# Revit family: Pump_Commercial-Effluent-Zoeller-6150_Seroes
name_source: partatom
category: Mechanical Equipment
revit_build: Autodesk Revit 2018 (Build: 20170223_1515(x64)
units: mm (PartAtom-declared; Revit-internal decimal feet)

## family parameters
Always vertical = No
Classification = None
Cut with Voids When Loaded = No
OmniClass Number = 23.60.30.21
OmniClass Title = Pumps
Part Type = Normal
Room Calculation Point = No
Round Connector Dimension = Use Radius
Shared = Yes
Work Plane-Based = Yes

## types (2) — shared parameters
Assembly Code = D2010900
Default Elevation = 0"
Description = Commercial Duty Pumps 6150 Series
Discharge Diameter = 1 1/2" NPT
Discharge Height = 5 3/8"
Discharge Radius = 3/4"
Height = 12 1/8"
Hertz = 60
Impeller Type = Plastic
Installation Type = Floor Mounted
Insulation = Class B
Lead Wires Insulation = Class B
Length = 10 3/32"
Manufacturer = Zoeller
Masterformat Number = 33 36 16
Masterformat Title = Utility Septic Tank Effluent Pumps
Material = Cast Iron-Zoeller-Powder Coated Epoxy
Max. Flow at Min. Head = 77 GPM @ 5' (291 L/min @ 1.5m)
Max. Water Temp. = 130 °F
Maximum Head = 528"
Minimum Head = 60"
Motor = 1/2 HP
Motor Design Letter = NEMA B
Motor Thermal Shutoff (Single Phase Only) = Standard
Motor Type = Submersible
Omniclass Table 23 Code = 23.60.30.21
Omniclass Table 23 Title = Pumps
Phase = 1
Price = Prices may vary. Please consult Manufacturer Representative for most up-to-date price list.
Product Page URL = https://www.zoellerengineered.com
Service Factor = 1.15
Shaft Seal = Standard
Solid Size = 3/4"
Square Ring & Gasket = Viton
Type SOW Power Cord Length = 240"
URL = http://www.zoellerengprod.com
Warranty Information = 36 Months (Limited)
Waste Connection = Yes
Width = 7 3/4"

## per-type parameters (varying)
| type | Amps (Voltage Dependent) | Model | Voltage |
| N6155 115V 1 PH | 10.5 | N6155 | 115V |
| E6155 230V 1PH | 5.3 | E6155 | 230 V |

## geometry (parser evidence)
native form markers: Sweep x2
no freeform markers — native parametric forms only
